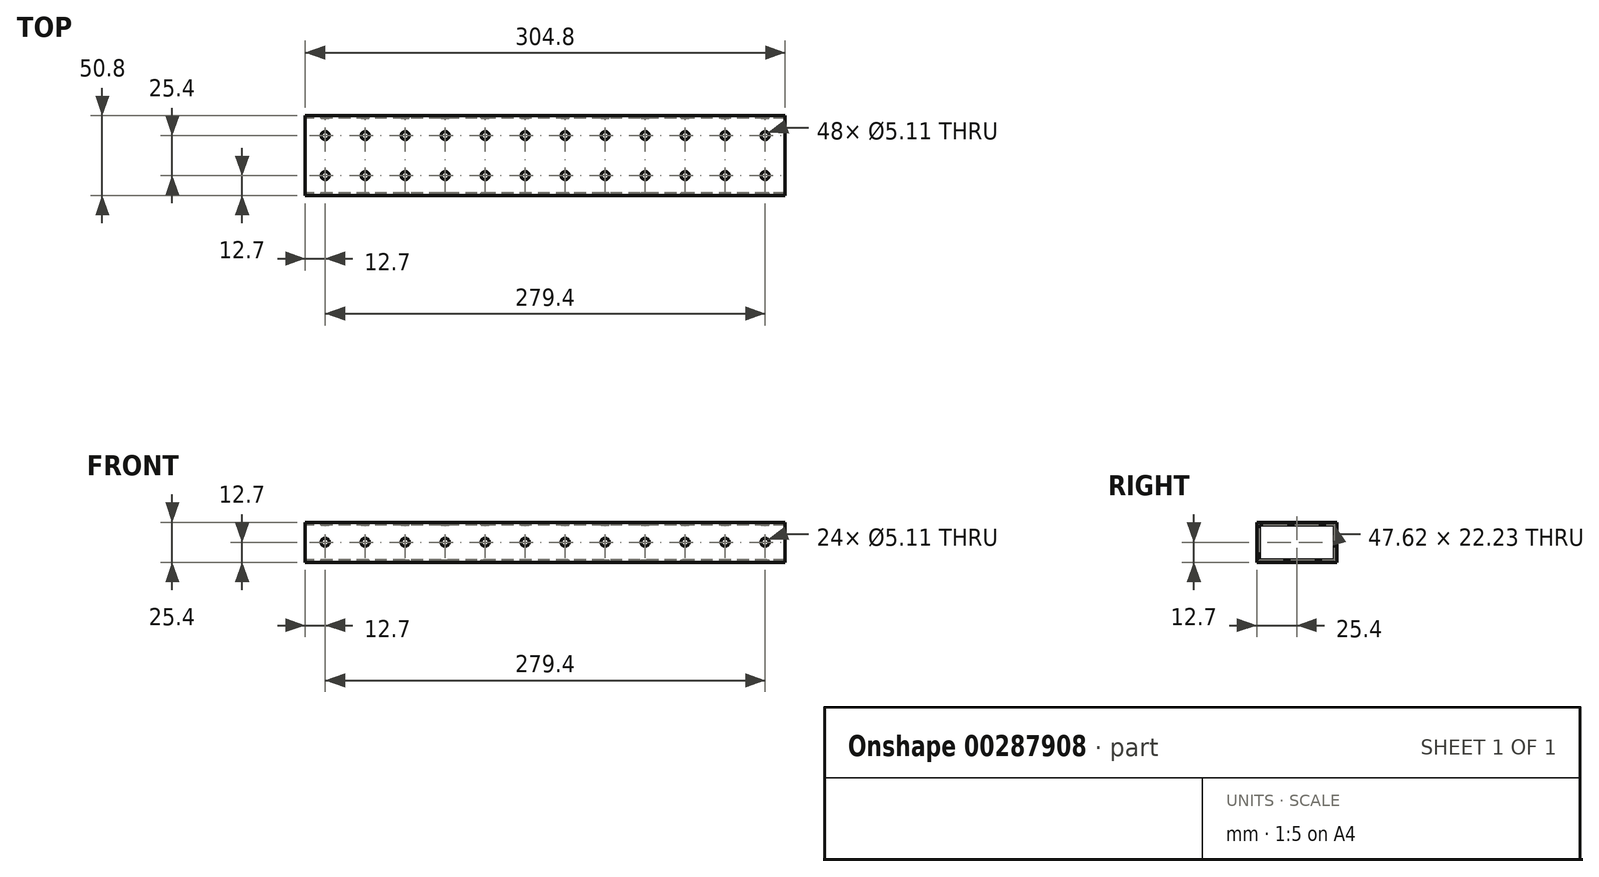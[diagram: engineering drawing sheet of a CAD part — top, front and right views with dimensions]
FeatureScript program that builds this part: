
annotation { "Feature Type Name" : "Feature", "Feature Type Description" : "" }
export const myFeature = defineFeature(function(context is Context, id is Id, definition is map)
    precondition{}
    {
        {
            var Q0;
            Q0=qCreatedBy(makeId("Right.planeOp"),FACE);
            var sketch = newSketch(context, id + "F0", { "sketchPlane" : qUnion([Q0])});
            skLineSegment(sketch, "E0.bottom", {"start": v(25.4, 12.7) * mm, "end": v(-25.4, 12.7) * mm});
            skLineSegment(sketch, "E0.top", {"start": v(25.4, -12.7) * mm, "end": v(-25.4, -12.7) * mm});
            skLineSegment(sketch, "E0.left", {"start": v(25.4, 12.7) * mm, "end": v(25.4, -12.7) * mm});
            skLineSegment(sketch, "E0.right", {"start": v(-25.4, 12.7) * mm, "end": v(-25.4, -12.7) * mm});
            skPoint(sketch, "E0.middle", {"position": v(0, 0) * mm});
            skLineSegment(sketch, "E1.bottom", {"start": v(23.81, 11.11) * mm, "end": v(-23.81, 11.11) * mm});
            skLineSegment(sketch, "E1.top", {"start": v(23.81, -11.11) * mm, "end": v(-23.81, -11.11) * mm});
            skLineSegment(sketch, "E1.left", {"start": v(23.81, 11.11) * mm, "end": v(23.81, -11.11) * mm});
            skLineSegment(sketch, "E1.right", {"start": v(-23.81, 11.11) * mm, "end": v(-23.81, -11.11) * mm});
            skSolve(sketch);
        }
        {
            var Q0;
            Q0=qSketchRegion(id+"F0",true);
            extrude(context, id + "F1", {"entities" : qUnion([Q0]), "depth" : 304.8 * mm});
        }
        {
            var Q0;
            Q0=makeQuery(id+"F1.opExtrude","SWEPT_FACE",FACE,{"disambiguationData":[OSD([sQuery(id+"F0.wireOp",EDGE,"E0.bottom")])]});
            var sketch = newSketch(context, id + "F2", { "sketchPlane" : qUnion([Q0])});
            skCircle(sketch, "E2", {"center": v(12.7, 12.7) * mm, "radius": 2.55 * mm});
            skCircle(sketch, "E3.0.1.0", {"center": v(12.7, -12.7) * mm, "radius": 2.55 * mm});
            skCircle(sketch, "E3.1.0.0", {"center": v(38.1, 12.7) * mm, "radius": 2.55 * mm});
            skCircle(sketch, "E3.1.1.0", {"center": v(38.1, -12.7) * mm, "radius": 2.55 * mm});
            skCircle(sketch, "E3.2.0.0", {"center": v(63.5, 12.7) * mm, "radius": 2.55 * mm});
            skCircle(sketch, "E3.2.1.0", {"center": v(63.5, -12.7) * mm, "radius": 2.55 * mm});
            skCircle(sketch, "E3.3.0.0", {"center": v(88.9, 12.7) * mm, "radius": 2.55 * mm});
            skCircle(sketch, "E3.3.1.0", {"center": v(88.9, -12.7) * mm, "radius": 2.55 * mm});
            skCircle(sketch, "E3.4.0.0", {"center": v(114.3, 12.7) * mm, "radius": 2.55 * mm});
            skCircle(sketch, "E3.4.1.0", {"center": v(114.3, -12.7) * mm, "radius": 2.55 * mm});
            skCircle(sketch, "E3.5.0.0", {"center": v(139.7, 12.7) * mm, "radius": 2.55 * mm});
            skCircle(sketch, "E3.5.1.0", {"center": v(139.7, -12.7) * mm, "radius": 2.55 * mm});
            skCircle(sketch, "E3.6.0.0", {"center": v(165.1, 12.7) * mm, "radius": 2.55 * mm});
            skCircle(sketch, "E3.6.1.0", {"center": v(165.1, -12.7) * mm, "radius": 2.55 * mm});
            skCircle(sketch, "E3.7.0.0", {"center": v(190.5, 12.7) * mm, "radius": 2.55 * mm});
            skCircle(sketch, "E3.7.1.0", {"center": v(190.5, -12.7) * mm, "radius": 2.55 * mm});
            skCircle(sketch, "E3.8.0.0", {"center": v(215.9, 12.7) * mm, "radius": 2.55 * mm});
            skCircle(sketch, "E3.8.1.0", {"center": v(215.9, -12.7) * mm, "radius": 2.55 * mm});
            skCircle(sketch, "E3.9.0.0", {"center": v(241.3, 12.7) * mm, "radius": 2.55 * mm});
            skCircle(sketch, "E3.9.1.0", {"center": v(241.3, -12.7) * mm, "radius": 2.55 * mm});
            skCircle(sketch, "E3.10.0.0", {"center": v(266.7, 12.7) * mm, "radius": 2.55 * mm});
            skCircle(sketch, "E3.10.1.0", {"center": v(266.7, -12.7) * mm, "radius": 2.55 * mm});
            skCircle(sketch, "E3.11.0.0", {"center": v(292.1, 12.7) * mm, "radius": 2.55 * mm});
            skCircle(sketch, "E3.11.1.0", {"center": v(292.1, -12.7) * mm, "radius": 2.55 * mm});
            skLineSegment(sketch, "E3.direction1", {"start": v(12.7, 12.7) * mm, "end": v(38.1, 12.7) * mm, "construction": true});
            skLineSegment(sketch, "E3.direction2", {"start": v(12.7, 12.7) * mm, "end": v(12.7, -12.7) * mm, "construction": true});
            skSolve(sketch);
        }
        {
            var Q0;
            Q0=sQuery(id+"F2.wireOp",VERTEX,"E3.1.1.0.center");
            var Q1;
            Q1=sQuery(id+"F2.wireOp",VERTEX,"E3.2.0.0.center");
            var Q2;
            Q2=sQuery(id+"F2.wireOp",VERTEX,"E3.2.1.0.center");
            var Q3;
            Q3=sQuery(id+"F2.wireOp",VERTEX,"E3.3.0.0.center");
            var Q4;
            Q4=sQuery(id+"F2.wireOp",VERTEX,"E3.3.1.0.center");
            var Q5;
            Q5=sQuery(id+"F2.wireOp",VERTEX,"E3.4.0.0.center");
            var Q6;
            Q6=sQuery(id+"F2.wireOp",VERTEX,"E3.11.1.0.center");
            var Q7;
            Q7=sQuery(id+"F2.wireOp",VERTEX,"E3.10.1.0.center");
            var Q8;
            Q8=sQuery(id+"F2.wireOp",VERTEX,"E3.9.1.0.center");
            var Q9;
            Q9=sQuery(id+"F2.wireOp",VERTEX,"E3.8.1.0.center");
            var Q10;
            Q10=sQuery(id+"F2.wireOp",VERTEX,"E3.7.1.0.center");
            var Q11;
            Q11=sQuery(id+"F2.wireOp",VERTEX,"E3.6.1.0.center");
            var Q12;
            Q12=sQuery(id+"F2.wireOp",VERTEX,"E3.11.0.0.center");
            var Q13;
            Q13=sQuery(id+"F2.wireOp",VERTEX,"E3.10.0.0.center");
            var Q14;
            Q14=sQuery(id+"F2.wireOp",VERTEX,"E3.9.0.0.center");
            var Q15;
            Q15=sQuery(id+"F2.wireOp",VERTEX,"E3.8.0.0.center");
            var Q16;
            Q16=sQuery(id+"F2.wireOp",VERTEX,"E3.4.1.0.center");
            var Q17;
            Q17=sQuery(id+"F2.wireOp",VERTEX,"E3.7.0.0.center");
            var Q18;
            Q18=sQuery(id+"F2.wireOp",VERTEX,"E3.5.0.0.center");
            var Q19;
            Q19=sQuery(id+"F2.wireOp",VERTEX,"E3.5.1.0.center");
            var Q20;
            Q20=sQuery(id+"F2.wireOp",VERTEX,"E3.6.0.0.center");
            var Q21;
            Q21=sQuery(id+"F2.wireOp",VERTEX,"E2.center");
            var Q22;
            Q22=sQuery(id+"F2.wireOp",VERTEX,"E3.0.1.0.center");
            var Q23;
            Q23=sQuery(id+"F2.wireOp",VERTEX,"E3.1.0.0.center");
            var Q24;
            Q24=makeQuery(id+"F1.opExtrude","SWEPT_BODY",BODY,{"disambiguationData":[OSD([sQuery(id+"F0.wireOp",EDGE,"E0.bottom"),sQuery(id+"F0.wireOp",EDGE,"E0.top"),sQuery(id+"F0.wireOp",EDGE,"E0.left"),sQuery(id+"F0.wireOp",EDGE,"E0.right"),sQuery(id+"F0.wireOp",EDGE,"E1.bottom"),sQuery(id+"F0.wireOp",EDGE,"E1.top"),sQuery(id+"F0.wireOp",EDGE,"E1.left"),sQuery(id+"F0.wireOp",EDGE,"E1.right")])]});
            hole(context, id + "F3", {"style" : HoleStyle.SIMPLE, "endStyle" : HoleEndStyle.THROUGH, "holeDiameter" : 5.1 * mm, "tappedDepth" : 12.7 * mm, "tapClearance" : 3, "locations" : qUnion([Q0, Q1, Q2, Q3, Q4, Q5, Q6, Q7, Q8, Q9, Q10, Q11, Q12, Q13, Q14, Q15, Q16, Q17, Q18, Q19, Q20, Q21, Q22, Q23]), "scope" : qUnion([Q24])});
        }
        {
            var Q0;
            Q0=makeQuery(id+"F1.opExtrude","SWEPT_FACE",FACE,{"disambiguationData":[OSD([sQuery(id+"F0.wireOp",EDGE,"E0.left")])]});
            var sketch = newSketch(context, id + "F4", { "sketchPlane" : qUnion([Q0])});
            skCircle(sketch, "E4", {"center": v(-292.1, 0) * mm, "radius": 2.55 * mm});
            skCircle(sketch, "E5.1.0.0", {"center": v(-266.7, 0) * mm, "radius": 2.55 * mm});
            skCircle(sketch, "E5.2.0.0", {"center": v(-241.3, 0) * mm, "radius": 2.55 * mm});
            skCircle(sketch, "E5.3.0.0", {"center": v(-215.9, 0) * mm, "radius": 2.55 * mm});
            skCircle(sketch, "E5.4.0.0", {"center": v(-190.5, 0) * mm, "radius": 2.55 * mm});
            skCircle(sketch, "E5.5.0.0", {"center": v(-165.1, 0) * mm, "radius": 2.55 * mm});
            skCircle(sketch, "E5.6.0.0", {"center": v(-139.7, 0) * mm, "radius": 2.55 * mm});
            skCircle(sketch, "E5.7.0.0", {"center": v(-114.3, 0) * mm, "radius": 2.55 * mm});
            skCircle(sketch, "E5.8.0.0", {"center": v(-88.9, 0) * mm, "radius": 2.55 * mm});
            skCircle(sketch, "E5.9.0.0", {"center": v(-63.5, 0) * mm, "radius": 2.55 * mm});
            skCircle(sketch, "E5.10.0.0", {"center": v(-38.1, 0) * mm, "radius": 2.55 * mm});
            skCircle(sketch, "E5.11.0.0", {"center": v(-12.7, 0) * mm, "radius": 2.55 * mm});
            skLineSegment(sketch, "E5.direction1", {"start": v(-292.1, 0) * mm, "end": v(-266.7, 0) * mm, "construction": true});
            skSolve(sketch);
        }
        {
            var Q0;
            Q0=sQuery(id+"F4.wireOp",VERTEX,"E5.3.0.0.center");
            var Q1;
            Q1=sQuery(id+"F4.wireOp",VERTEX,"E5.2.0.0.center");
            var Q2;
            Q2=sQuery(id+"F4.wireOp",VERTEX,"E5.4.0.0.center");
            var Q3;
            Q3=sQuery(id+"F4.wireOp",VERTEX,"E5.6.0.0.center");
            var Q4;
            Q4=sQuery(id+"F4.wireOp",VERTEX,"E5.5.0.0.center");
            var Q5;
            Q5=sQuery(id+"F4.wireOp",VERTEX,"E5.8.0.0.center");
            var Q6;
            Q6=sQuery(id+"F4.wireOp",VERTEX,"E5.7.0.0.center");
            var Q7;
            Q7=sQuery(id+"F4.wireOp",VERTEX,"E5.1.0.0.center");
            var Q8;
            Q8=sQuery(id+"F4.wireOp",VERTEX,"E4.center");
            var Q9;
            Q9=sQuery(id+"F4.wireOp",VERTEX,"E5.11.0.0.center");
            var Q10;
            Q10=sQuery(id+"F4.wireOp",VERTEX,"E5.10.0.0.center");
            var Q11;
            Q11=sQuery(id+"F4.wireOp",VERTEX,"E5.9.0.0.center");
            var Q12;
            Q12=makeQuery(id+"F1.opExtrude","SWEPT_BODY",BODY,{"disambiguationData":[OSD([sQuery(id+"F0.wireOp",EDGE,"E0.bottom"),sQuery(id+"F0.wireOp",EDGE,"E0.top"),sQuery(id+"F0.wireOp",EDGE,"E0.left"),sQuery(id+"F0.wireOp",EDGE,"E0.right"),sQuery(id+"F0.wireOp",EDGE,"E1.bottom"),sQuery(id+"F0.wireOp",EDGE,"E1.top"),sQuery(id+"F0.wireOp",EDGE,"E1.left"),sQuery(id+"F0.wireOp",EDGE,"E1.right")])]});
            hole(context, id + "F5", {"style" : HoleStyle.SIMPLE, "endStyle" : HoleEndStyle.THROUGH, "holeDiameter" : 5.1 * mm, "tappedDepth" : 12.7 * mm, "tapClearance" : 3, "locations" : qUnion([Q0, Q1, Q2, Q3, Q4, Q5, Q6, Q7, Q8, Q9, Q10, Q11]), "scope" : qUnion([Q12])});
        }
    });
